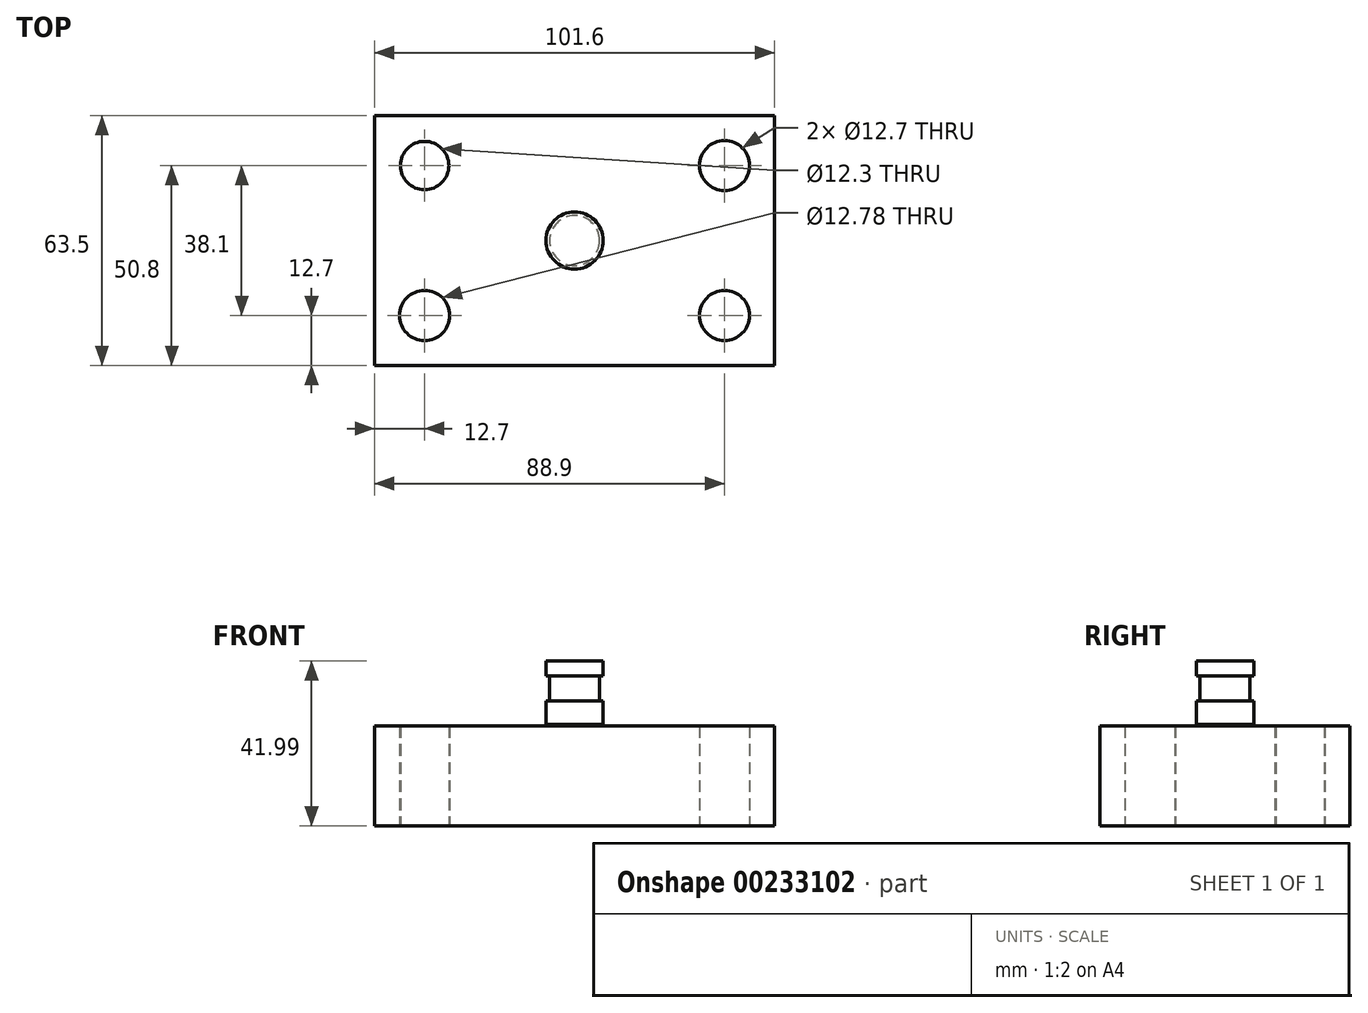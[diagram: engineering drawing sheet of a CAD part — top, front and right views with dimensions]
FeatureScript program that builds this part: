
annotation { "Feature Type Name" : "Feature", "Feature Type Description" : "" }
export const myFeature = defineFeature(function(context is Context, id is Id, definition is map)
    precondition{}
    {
        {
            var Q0;
            Q0=qCreatedBy(makeId("Top.planeOp"),FACE);
            var sketch = newSketch(context, id + "F0", { "sketchPlane" : qUnion([Q0])});
            skLineSegment(sketch, "E0.bottom", {"start": v(50.8, 31.75) * mm, "end": v(-50.8, 31.75) * mm});
            skLineSegment(sketch, "E0.top", {"start": v(50.8, -31.75) * mm, "end": v(-50.8, -31.75) * mm});
            skLineSegment(sketch, "E0.left", {"start": v(50.8, 31.75) * mm, "end": v(50.8, -31.75) * mm});
            skLineSegment(sketch, "E0.right", {"start": v(-50.8, 31.75) * mm, "end": v(-50.8, -31.75) * mm});
            skPoint(sketch, "E0.middle", {"position": v(0, 0) * mm});
            skSolve(sketch);
        }
        {
            var Q0;
            Q0=makeQuery(id+"F0.imprint","IMPRINT",FACE,{"disambiguationData":[TD([[makeQuery(id+"F0.imprint","IMPRINT",EDGE,{"derivedFrom":sQuery(id+"F0.wireOp",EDGE,"E0.bottom")}),1.0]])]});
            extrude(context, id + "F1", {"entities" : qUnion([Q0]), "depth" : 25.4 * mm});
        }
        {
            var Q0;
            Q0=qCreatedBy(makeId("Top.planeOp"),FACE);
            var sketch = newSketch(context, id + "F2", { "sketchPlane" : qUnion([Q0])});
            skCircle(sketch, "E1", {"center": v(38.1, -19.05) * mm, "radius": 6.35 * mm});
            skCircle(sketch, "E2", {"center": v(38.1, 19.05) * mm, "radius": 6.35 * mm});
            skCircle(sketch, "E3", {"center": v(-38.1, 19.05) * mm, "radius": 6.15 * mm});
            skCircle(sketch, "E4", {"center": v(-38.1, -19.05) * mm, "radius": 6.4 * mm});
            skSolve(sketch);
        }
        {
            var Q0;
            Q0 = qSketchRegion(id + "F2", true);
            extrude(context, id + "F3", {"entities" : qUnion([Q0]), "operationType" : NewBodyOperationType.REMOVE, "endBound" : BoundingType.THROUGH_ALL, "depth" : 25.4 * mm});
        }
        {
            var Q0;
            Q0=qCreatedBy(makeId("Right.planeOp"),FACE);
            var sketch = newSketch(context, id + "F4", { "sketchPlane" : qUnion([Q0])});
            skLineSegment(sketch, "E5.bottom", {"start": v(0, 25.76) * mm, "end": v(-7.27, 25.76) * mm});
            skLineSegment(sketch, "E5.top", {"start": v(0, 41.99) * mm, "end": v(-7.27, 41.99) * mm});
            skLineSegment(sketch, "E5.left", {"start": v(0, 25.76) * mm, "end": v(0, 41.99) * mm});
            skLineSegment(sketch, "E5.right", {"start": v(-7.27, 25.76) * mm, "end": v(-7.27, 41.99) * mm});
            skSolve(sketch);
        }
        {
            var Q0;
            Q0 = qSketchRegion(id + "F4", true);
            var Q1;
            Q1=sQuery(id+"F4.wireOp",EDGE,"E5.left");
            revolve(context, id + "F5", {"entities" : qUnion([Q0]), "axis" : qUnion([Q1]), "revolveType" : RevolveType.FULL});
        }
        {
            var Q0;
            Q0=qCreatedBy(makeId("Front.planeOp"),FACE);
            var sketch = newSketch(context, id + "F6", { "sketchPlane" : qUnion([Q0])});
            skLineSegment(sketch, "E6.bottom", {"start": v(-6.35, 38.1) * mm, "end": v(-11.24, 38.1) * mm});
            skLineSegment(sketch, "E6.top", {"start": v(-6.35, 31.75) * mm, "end": v(-11.24, 31.75) * mm});
            skLineSegment(sketch, "E6.left", {"start": v(-6.35, 38.1) * mm, "end": v(-6.35, 31.75) * mm});
            skLineSegment(sketch, "E6.right", {"start": v(-11.24, 38.1) * mm, "end": v(-11.24, 31.75) * mm});
            skSolve(sketch);
        }
        {
            var Q0;
            Q0=makeQuery(id+"F6.imprint","IMPRINT",FACE,{"disambiguationData":[TD([[makeQuery(id+"F6.imprint","IMPRINT",EDGE,{"derivedFrom":sQuery(id+"F6.wireOp",EDGE,"E6.bottom")}),1.0]])]});
            var Q1;
            Q1=makeQuery(id+"F5.opRevolve","SWEPT_FACE",FACE,{"disambiguationData":[OSD([sQuery(id+"F4.wireOp",EDGE,"E5.right")])]});
            revolve(context, id + "F7", {"operationType" : NewBodyOperationType.REMOVE, "entities" : qUnion([Q0]), "axis" : qUnion([Q1]), "revolveType" : RevolveType.FULL, "oppositeDirection" : true});
        }
    });
